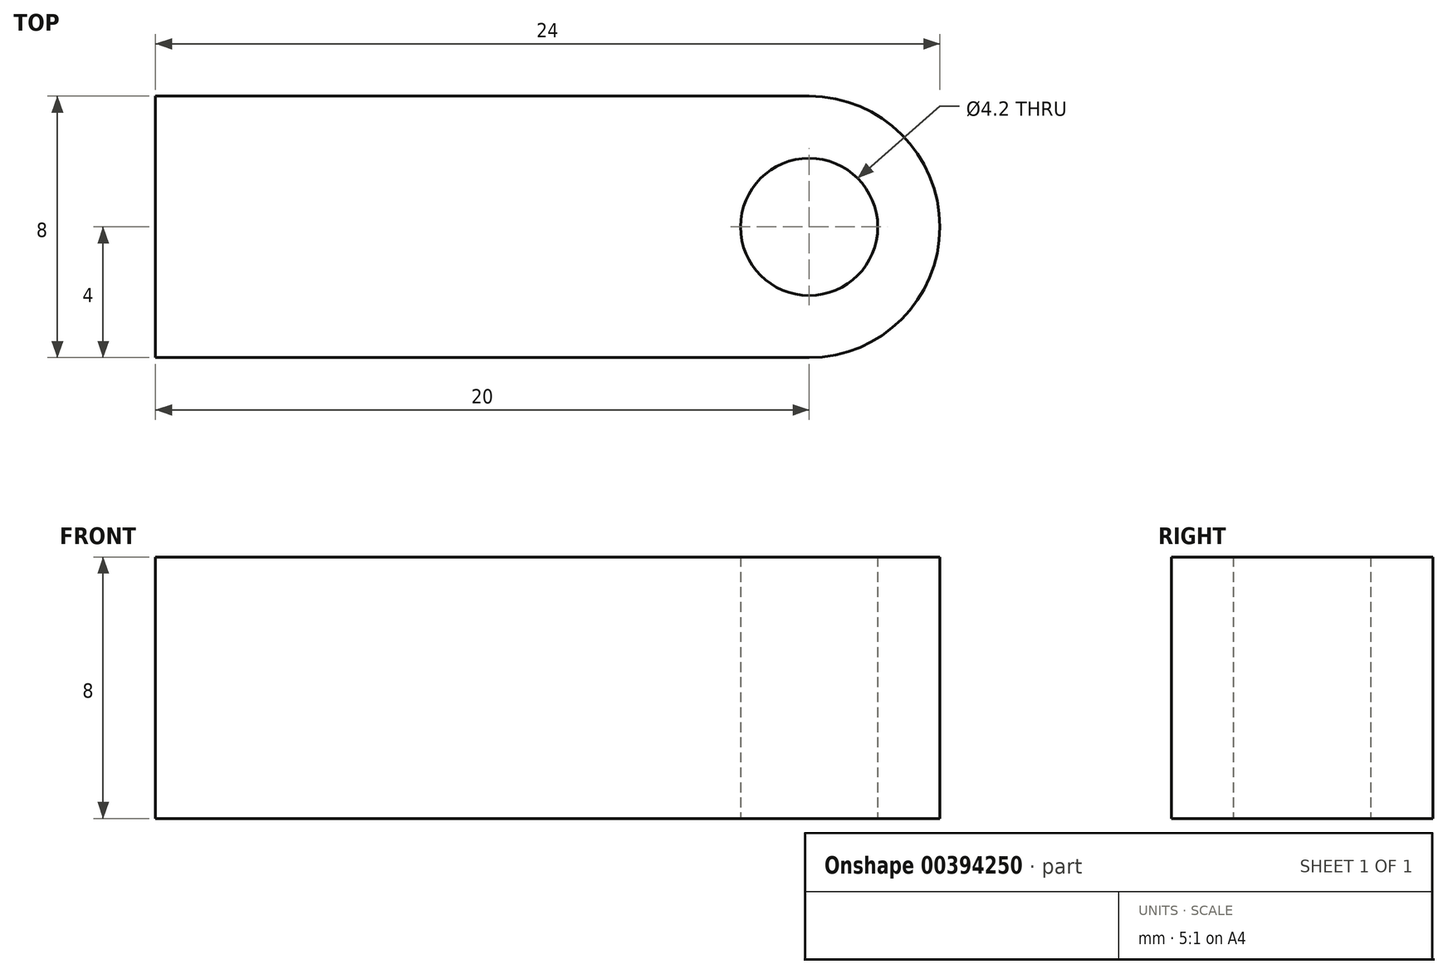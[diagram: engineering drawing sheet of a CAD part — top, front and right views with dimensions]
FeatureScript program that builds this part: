
annotation { "Feature Type Name" : "Feature", "Feature Type Description" : "" }
export const myFeature = defineFeature(function(context is Context, id is Id, definition is map)
    precondition{}
    {
        {
            var Q0;
            Q0=qCreatedBy(makeId("Top.planeOp"),FACE);
            var sketch = newSketch(context, id + "F0", { "sketchPlane" : qUnion([Q0])});
            skCircle(sketch, "E0", {"center": v(0, 0) * mm, "radius": 2.1 * mm});
            skArc(sketch, "E1", {"start": v(0, -4) * mm, "mid": v(4, 0) * mm, "end": v(0, 4) * mm});
            skLineSegment(sketch, "E2", {"start": v(0, 4) * mm, "end": v(-20, 4) * mm});
            skLineSegment(sketch, "E3", {"start": v(-20, 4) * mm, "end": v(-20, -4) * mm});
            skLineSegment(sketch, "E4", {"start": v(-20, -4) * mm, "end": v(0, -4) * mm});
            skSolve(sketch);
        }
        {
            var Q0;
            Q0 = qSketchRegion(id + "F0", true);
            extrude(context, id + "F1", {"entities" : qUnion([Q0]), "endBound" : BoundingType.SYMMETRIC, "depth" : 8 * mm});
        }
    });
